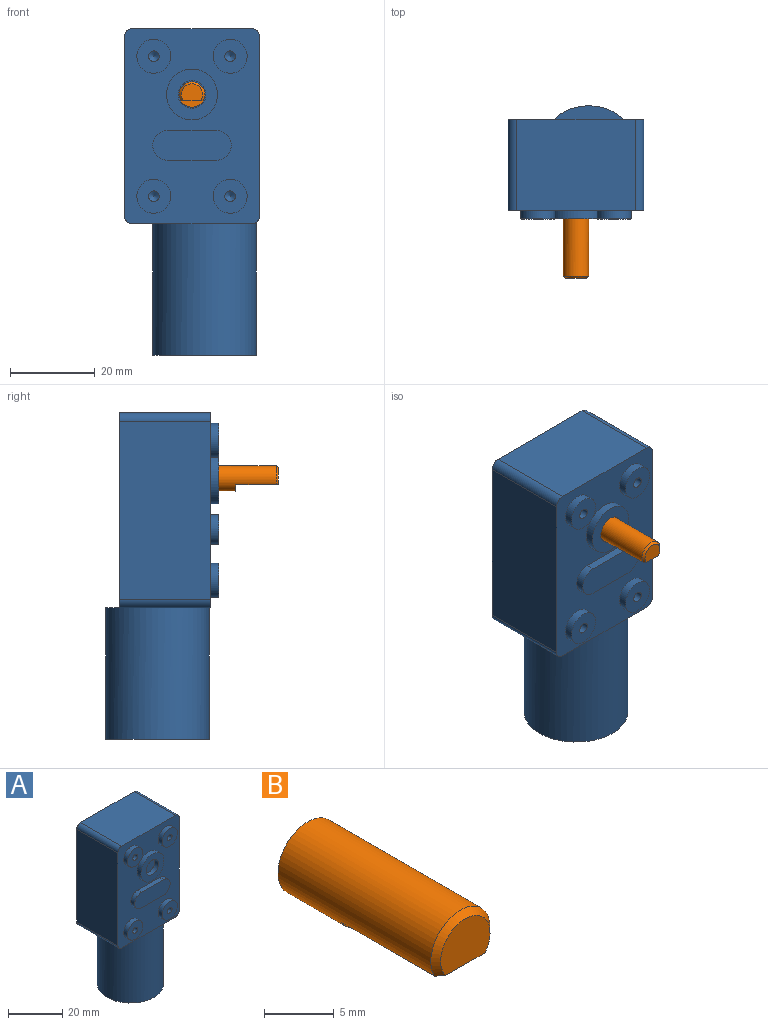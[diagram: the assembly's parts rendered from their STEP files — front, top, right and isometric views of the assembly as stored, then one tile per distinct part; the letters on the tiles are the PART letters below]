
ASSEMBLY  parts=2 mates=1
PART A: 40 faces, bbox 32x26.7x77 mm
  f0: plane 3.72x2.76mm, normal (0,0,-1), area 4.5mm2, adj f8,f9,f29
  f1: plane 42x21.5mm, normal (1,0,0), area 903mm2, adj f2,f8,f9,f10
  f2: cylinder r=2mm len=21.5mm, axis (0,-1,0), area 67.5mm2, adj f1,f3,f9,f10
  f3: plane 28x21.5mm, normal (0,0,1), area 602mm2, adj f2,f4,f9,f10
  f4: cylinder r=2mm len=21.5mm, axis (0,-1,0), area 67.5mm2, adj f3,f5,f9,f10
  f5: plane 42x21.5mm, normal (-1,0,0), area 903mm2, adj f4,f6,f9,f10
  f6: cylinder r=2mm len=21.5mm, axis (0,-1,0), area 67.5mm2, adj f5,f7,f9,f10
  f7: plane 28x21.5mm, normal (0,0,-1), area 174.7mm2, adj f6,f8,f9,f10,f29
  f8: cylinder r=2mm len=21.5mm, axis (0,-1,0), area 67.5mm2, adj f0,f1,f7,f9,f10,f31
  f9: plane 46x32mm, normal (0,1,0), area 1468.6mm2, adj f0,f1,f2,f3,f4,f5,f6,f7
  f10: plane 46x32mm, normal (0,-1,0), area 1035.4mm2, adj f1,f2,f3,f4,f5,f6,f7,f8
  f11: cylinder r=4mm len=8mm, axis (0,1,0), area 50.3mm2, adj f10,f12
  f12: plane 8x8mm, normal (0,-1,0), area 45.4mm2, adj f11,f39
  f13: cylinder r=4mm len=8mm, axis (0,1,0), area 50.3mm2, adj f10,f14
  f14: plane 8x8mm, normal (0,-1,0), area 45.4mm2, adj f13,f37
  f15: cylinder r=4mm len=8mm, axis (0,1,0), area 50.3mm2, adj f10,f16
  f16: plane 8x8mm, normal (0,-1,0), area 45.4mm2, adj f15,f35
  f17: cylinder r=4mm len=8mm, axis (0,1,0), area 50.3mm2, adj f10,f18
  f18: plane 8x8mm, normal (0,-1,0), area 45.4mm2, adj f17,f33
  f19: cylinder r=3.25mm len=6.5mm, axis (0,1,0), area 40.8mm2, adj f21,f22
  f20: cylinder r=6mm len=12mm, axis (0,1,0), area 75.4mm2, adj f10,f21
  f21: plane 12x12mm, normal (0,-1,0), area 79.9mm2, adj f19,f20
  f22: plane 6.5x6.5mm, normal (0,-1,0), area 33.2mm2, adj f19
  f23: plane 11.5x2mm, normal (0,0,1), area 23mm2, adj f10,f24,f26,f27
  f24: cylinder r=3.5mm len=7mm, axis (0,1,0), area 22mm2, adj f10,f23,f25,f27
  f25: plane 11.5x2mm, normal (0,0,-1), area 23mm2, adj f10,f24,f26,f27
  f26: cylinder r=3.5mm len=7mm, axis (0,1,0), area 22mm2, adj f10,f23,f25,f27
  f27: plane 18.5x7mm, normal (0,-1,0), area 119mm2, adj f23,f24,f25,f26
  f28: plane 16.47x3.2mm, normal (0,0,1), area 36.2mm2, adj f9,f29
  f29: cylinder r=12.2mm len=31mm, axis (0,0,1), area 2376.3mm2, adj f0,f7,f28,f30,f31
  f30: plane 24.4x24.4mm, normal (0,0,-1), area 467.6mm2, adj f29
  f31: plane 10.55x1.2mm, normal (0,0,1), area 8.5mm2, adj f8,f29
  f32: cone r=0mm half-angle=59deg, axis (0,-1,0), area 5.7mm2, adj f33
  f33: cylinder r=1.25mm len=6.5mm, axis (0,-1,0), area 51.1mm2, adj f18,f32
  f34: cone r=0mm half-angle=59deg, axis (0,-1,0), area 5.7mm2, adj f35
  f35: cylinder r=1.25mm len=6.5mm, axis (0,-1,0), area 51.1mm2, adj f16,f34
  f36: cone r=0mm half-angle=59deg, axis (0,-1,0), area 5.7mm2, adj f37
  f37: cylinder r=1.25mm len=6.5mm, axis (0,-1,0), area 51.1mm2, adj f14,f36
  f38: cone r=0mm half-angle=59deg, axis (0,-1,0), area 5.7mm2, adj f39
  f39: cylinder r=1.25mm len=6.5mm, axis (0,-1,0), area 51.1mm2, adj f12,f38
PART B: 6 faces, bbox 6x16x6 mm
  f0: cylinder r=3mm len=15.5mm, axis (0,1,0), area 232.5mm2, adj f2,f3,f4,f5
  f1: plane 5x4mm, normal (0,-1,0), area 16.8mm2, adj f4,f5
  f2: plane 6x6mm, normal (0,1,0), area 28.3mm2, adj f0
  f3: plane 5.2x1.5mm, normal (0,-1,0), area 5.5mm2, adj f0,f4
  f4: plane 10x5.2mm, normal (0,0,-1), area 51.7mm2, adj f0,f1,f3,f5
  f5: cone r=2.5mm half-angle=45deg, axis (0,1,0), area 8.4mm2, adj f0,f1,f4
PLACE A at identity fixed
PLACE B at identity
MATE revolute A.f19 <-> B.f0  axis (0,-1,0) through (0,0,0)mm
